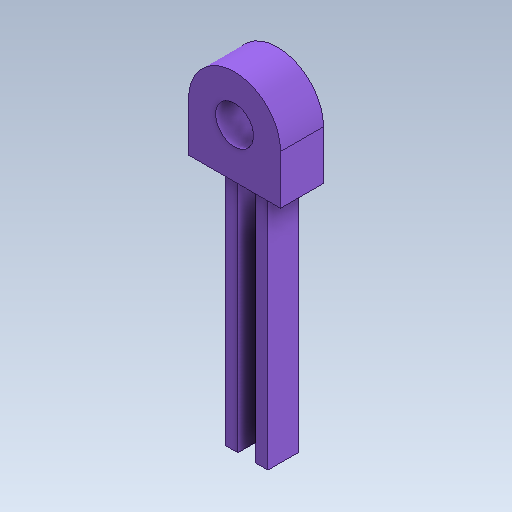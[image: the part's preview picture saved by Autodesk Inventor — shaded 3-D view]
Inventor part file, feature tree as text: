
AUTODESK INVENTOR PART (.ipt)
format: ipt  version: 2020 (Build 240168000, 168)  size: 227,840 bytes
history: native  units: in
note: dims shown in document units (in); Inventor stores cm internally (conversion verified against a paired STEP export)
features: extrude x8, sketch x8, projected_geometry x8
ambient origin geometry x8: Origin, YZ Plane, XZ Plane, XY Plane, X Axis, Y Axis, Z Axis, Center Point
bodies: Solid1 (feature_tree)
feature tree (24):
  extrude  "Extrusion1"  Depth=0.1358in
  extrude  "Extrusion4"  Depth=0.2894in
  extrude  "Extrusion5"  Depth=0.1378in TaperAngle=0.0deg
  extrude  "Extrusion6"  Depth=0.0797in
  extrude  "Extrusion7"  Depth=0.2953in
  extrude  "Extrusion8"  Depth=0.0787in TaperAngle=0.0deg
  extrude  "Extrusion9"  Depth=0.0394in
  extrude  "Extrusion11"  Depth=0.0394in TaperAngle=0.0deg
  sketch  "Sketch1"  dims[d0=0.7874in d1=0.1358in]
  sketch  "Sketch4"  dims[d2=0.1457in d3=0.2894in]
  projected_geometry  "Projected Loop3"
  sketch  "Sketch5"  dims[d4=0.1969in d5=0.1378in d6=0.0in]
  projected_geometry  "Projected Loop4"
  sketch  "Sketch6"  dims[d22=0.0797in d23=0.0797in]
  projected_geometry  "Projected Loop5"
  sketch  "Sketch7"  dims[d24=0.2953in d25=0.1575in]
  projected_geometry  "Projected Loop6"
  sketch  "Sketch8"  dims[d26=0.122in d27=0.0787in d28=0.0in]
  projected_geometry  "Projected Loop7"
  sketch  "Sketch9"  dims[d31=0.0394in d32=0.0394in]
  projected_geometry  "Projected Loop8"
  projected_geometry  "Projected Loop9"
  sketch  "Sketch11"  dims[d33=0.0689in d34=0.0in d35=0.0689in d36=0.0in d37=0.0197in d38=0.3937in d39=0.0in d40=0.7874in d41=0.0in d42=0.7874in d43=0.0in d46=0.0394in d47=0.0in]
  projected_geometry  "Projected Loop11"
